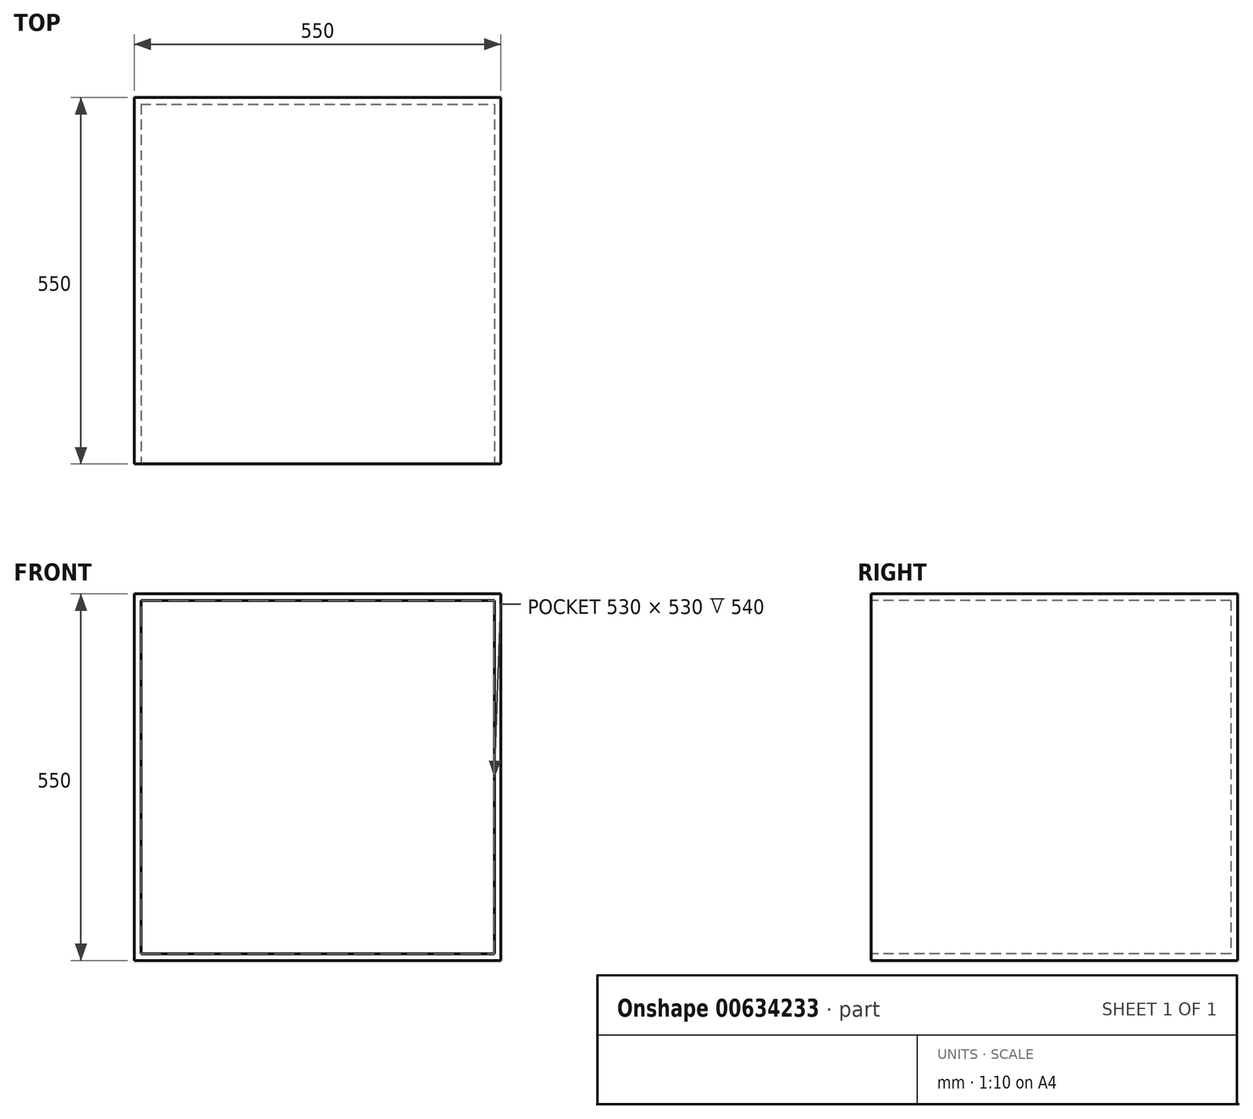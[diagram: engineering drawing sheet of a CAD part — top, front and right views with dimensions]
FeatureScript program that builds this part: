
annotation { "Feature Type Name" : "Feature", "Feature Type Description" : "" }
export const myFeature = defineFeature(function(context is Context, id is Id, definition is map)
    precondition{}
    {
        {
            var Q0;
            Q0=qCreatedBy(makeId("Top.planeOp"),FACE);
            var sketch = newSketch(context, id + "F0", { "sketchPlane" : qUnion([Q0])});
            skLineSegment(sketch, "E0.bottom", {"start": v(-511.36, 528.18) * mm, "end": v(38.64, 528.18) * mm});
            skLineSegment(sketch, "E0.top", {"start": v(-511.36, -21.82) * mm, "end": v(38.64, -21.82) * mm});
            skLineSegment(sketch, "E0.left", {"start": v(-511.36, 528.18) * mm, "end": v(-511.36, -21.82) * mm});
            skLineSegment(sketch, "E0.right", {"start": v(38.64, 528.18) * mm, "end": v(38.64, -21.82) * mm});
            skSolve(sketch);
        }
        {
            var Q0;
            Q0=makeQuery(id+"F0.imprint","IMPRINT",FACE,{"disambiguationData":[TD([[makeQuery(id+"F0.imprint","IMPRINT",EDGE,{"derivedFrom":sQuery(id+"F0.wireOp",EDGE,"E0.bottom")}),-1.0]])]});
            extrude(context, id + "F1", {"entities" : qUnion([Q0]), "oppositeDirection" : true, "depth" : 550 * mm, "offsetDistance" : 25 * mm});
        }
        {
            var Q0;
            Q0=makeQuery(id+"F1.opExtrude","SWEPT_FACE",FACE,{"disambiguationData":[OSD([sQuery(id+"F0.wireOp",EDGE,"E0.top")])]});
            var sketch = newSketch(context, id + "F2", { "sketchPlane" : qUnion([Q0])});
            skLineSegment(sketch, "E1.bottom", {"start": v(-501.36, -10) * mm, "end": v(28.64, -10) * mm});
            skLineSegment(sketch, "E1.top", {"start": v(-501.36, -540) * mm, "end": v(28.64, -540) * mm});
            skLineSegment(sketch, "E1.left", {"start": v(-501.36, -10) * mm, "end": v(-501.36, -540) * mm});
            skLineSegment(sketch, "E1.right", {"start": v(28.64, -10) * mm, "end": v(28.64, -540) * mm});
            skSolve(sketch);
        }
        {
            var Q0;
            Q0=makeQuery(id+"F2.imprint","IMPRINT",FACE,{"disambiguationData":[TD([[makeQuery(id+"F2.imprint","IMPRINT",EDGE,{"derivedFrom":sQuery(id+"F2.wireOp",EDGE,"E1.bottom")}),-1.0]])]});
            extrude(context, id + "F3", {"entities" : qUnion([Q0]), "operationType" : NewBodyOperationType.REMOVE, "oppositeDirection" : true, "depth" : 540 * mm, "offsetDistance" : 25 * mm});
        }
    });
